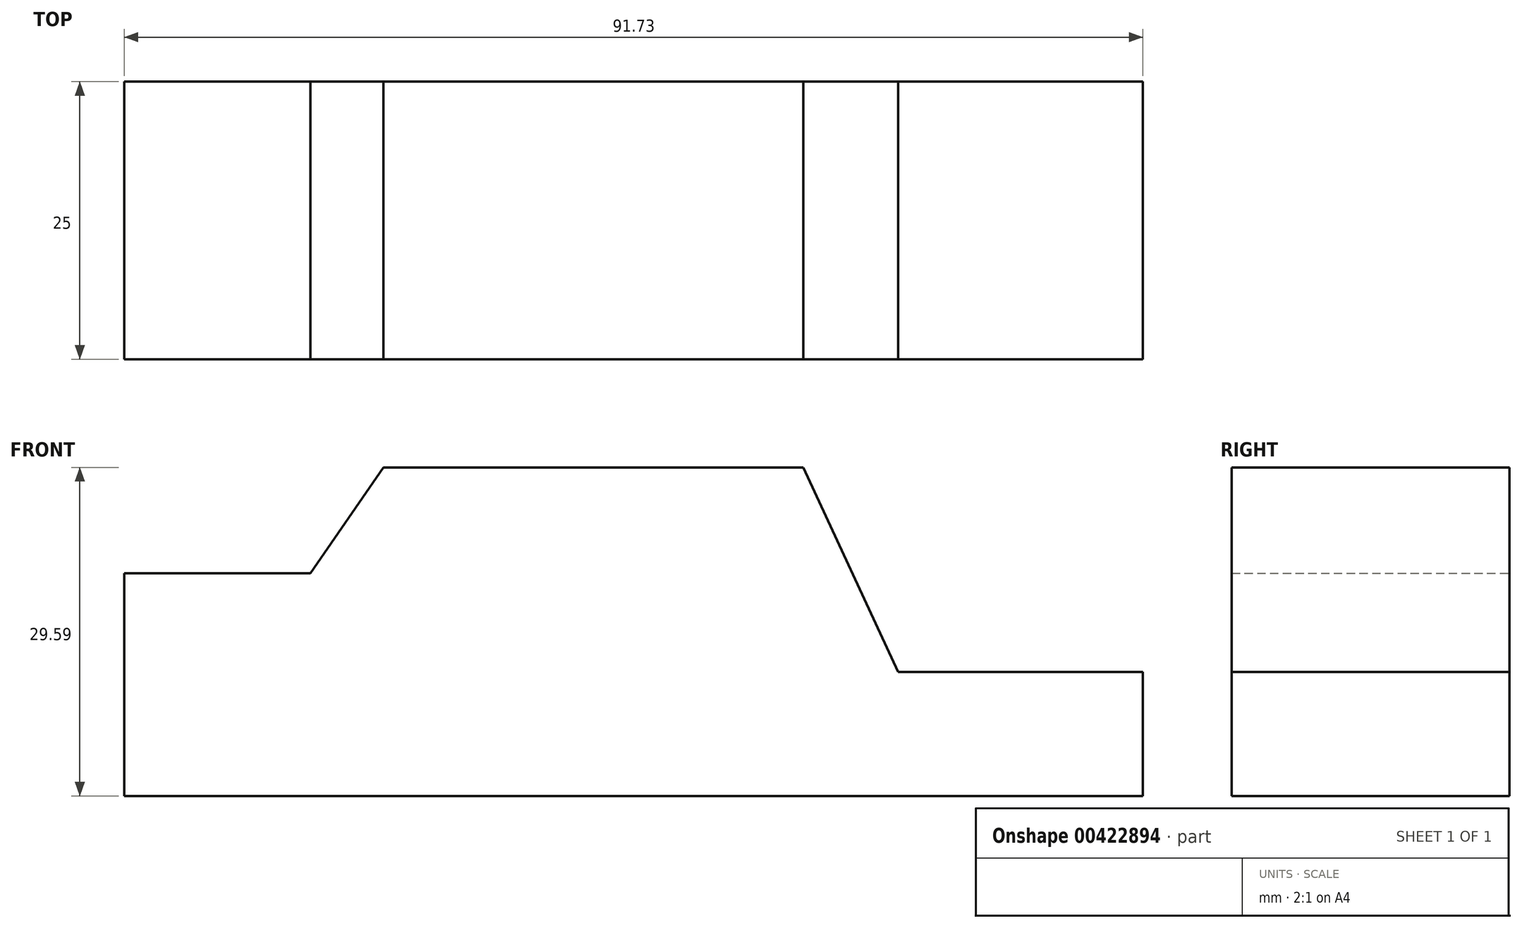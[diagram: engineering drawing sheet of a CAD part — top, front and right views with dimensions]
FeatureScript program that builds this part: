
annotation { "Feature Type Name" : "Feature", "Feature Type Description" : "" }
export const myFeature = defineFeature(function(context is Context, id is Id, definition is map)
    precondition{}
    {
        {
            var Q0;
            Q0=qCreatedBy(makeId("Front.planeOp"),FACE);
            var sketch = newSketch(context, id + "F0", { "sketchPlane" : qUnion([Q0])});
            skLineSegment(sketch, "E0", {"start": v(-49, 0) * mm, "end": v(-49, 20.06) * mm});
            skLineSegment(sketch, "E1", {"start": v(-49, 20.06) * mm, "end": v(-32.22, 20.06) * mm});
            skLineSegment(sketch, "E2", {"start": v(-32.22, 20.06) * mm, "end": v(-25.65, 29.6) * mm});
            skLineSegment(sketch, "E3", {"start": v(-25.65, 29.6) * mm, "end": v(12.17, 29.6) * mm});
            skLineSegment(sketch, "E4", {"start": v(12.17, 29.6) * mm, "end": v(20.71, 11.18) * mm});
            skLineSegment(sketch, "E5", {"start": v(20.71, 11.18) * mm, "end": v(42.74, 11.18) * mm});
            skLineSegment(sketch, "E6", {"start": v(42.74, 11.18) * mm, "end": v(42.74, 0) * mm});
            skLineSegment(sketch, "E7", {"start": v(42.74, 0) * mm, "end": v(-49, 0) * mm});
            skSolve(sketch);
        }
        {
            var Q0;
            Q0 = qSketchRegion(id + "F0", true);
            extrude(context, id + "F1", {"entities" : qUnion([Q0]), "depth" : 25 * mm});
        }
    });
